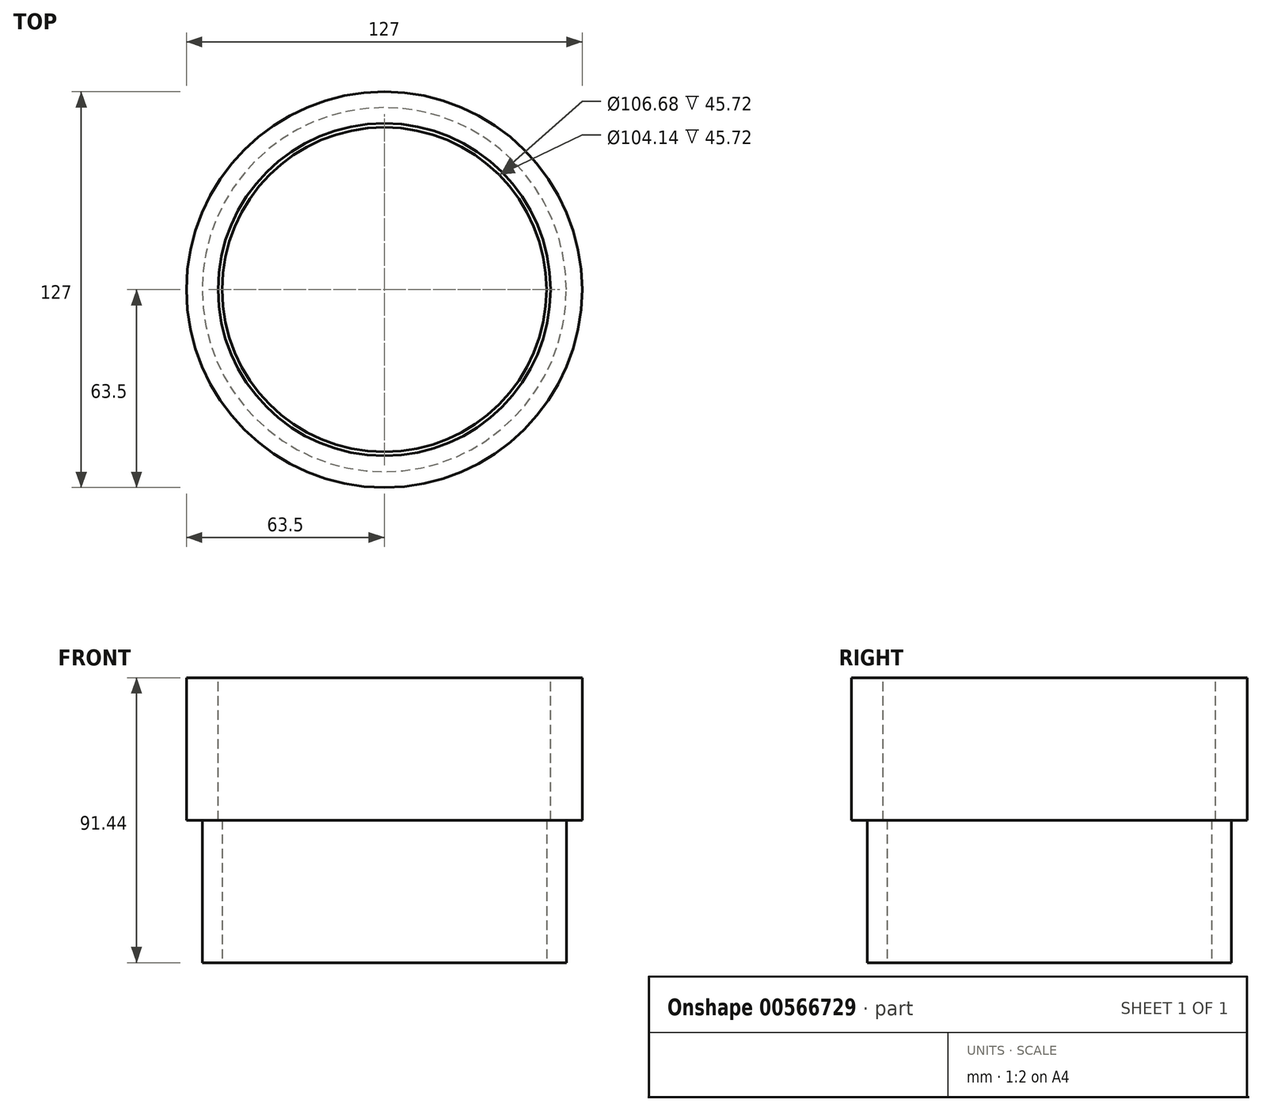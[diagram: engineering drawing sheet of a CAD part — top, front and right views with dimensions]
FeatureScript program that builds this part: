
annotation { "Feature Type Name" : "Feature", "Feature Type Description" : "" }
export const myFeature = defineFeature(function(context is Context, id is Id, definition is map)
    precondition{}
    {
        {
            var Q0;
            Q0=qCreatedBy(makeId("Top.planeOp"),FACE);
            var sketch = newSketch(context, id + "F0", { "sketchPlane" : qUnion([Q0])});
            skCircle(sketch, "E0", {"center": v(0, 0) * mm, "radius": 63.5 * mm});
            skSolve(sketch);
        }
        {
            var Q0;
            Q0 = qSketchRegion(id + "F0", true);
            extrude(context, id + "F1", {"entities" : qUnion([Q0]), "depth" : 45.72 * mm, "offsetDistance" : 25.4 * mm});
        }
        {
            var Q0;
            Q0=makeQuery(id+"F1.opExtrude","CAP_FACE",FACE,{"disambiguationData":[OSD([sQuery(id+"F0.wireOp",EDGE,"E0")])],"isStart":false});
            var sketch = newSketch(context, id + "F2", { "sketchPlane" : qUnion([Q0])});
            skCircle(sketch, "E1", {"center": v(0, 0) * mm, "radius": 53.34 * mm});
            skSolve(sketch);
        }
        {
            var Q0;
            Q0=makeQuery(id+"F2.imprint","IMPRINT",FACE,{"disambiguationData":[TD([[makeQuery(id+"F2.imprint","IMPRINT",EDGE,{"derivedFrom":sQuery(id+"F2.wireOp",EDGE,"E1")}),1.0]])]});
            extrude(context, id + "F3", {"entities" : qUnion([Q0]), "operationType" : NewBodyOperationType.REMOVE, "oppositeDirection" : true, "depth" : 50.8 * mm, "offsetDistance" : 25.4 * mm});
        }
        {
            var Q0;
            Q0=qCreatedBy(makeId("Top.planeOp"),FACE);
            var sketch = newSketch(context, id + "F4", { "sketchPlane" : qUnion([Q0])});
            skCircle(sketch, "E2", {"center": v(0, 0) * mm, "radius": 58.42 * mm});
            skSolve(sketch);
        }
        {
            var Q0;
            Q0 = qSketchRegion(id + "F4", true);
            extrude(context, id + "F5", {"entities" : qUnion([Q0]), "operationType" : NewBodyOperationType.ADD, "depth" : -45.72 * mm, "offsetDistance" : 25.4 * mm});
        }
        {
            var Q0;
            Q0=makeQuery(id+"F5.opExtrude","CAP_FACE",FACE,{"disambiguationData":[OSD([sQuery(id+"F4.wireOp",EDGE,"E2")])],"isStart":false});
            var sketch = newSketch(context, id + "F6", { "sketchPlane" : qUnion([Q0])});
            skCircle(sketch, "E3", {"center": v(0, 0) * mm, "radius": 52.07 * mm});
            skSolve(sketch);
        }
        {
            var Q0;
            Q0 = qSketchRegion(id + "F6", true);
            extrude(context, id + "F7", {"entities" : qUnion([Q0]), "operationType" : NewBodyOperationType.REMOVE, "oppositeDirection" : true, "depth" : 127 * mm, "offsetDistance" : 25.4 * mm});
        }
    });
